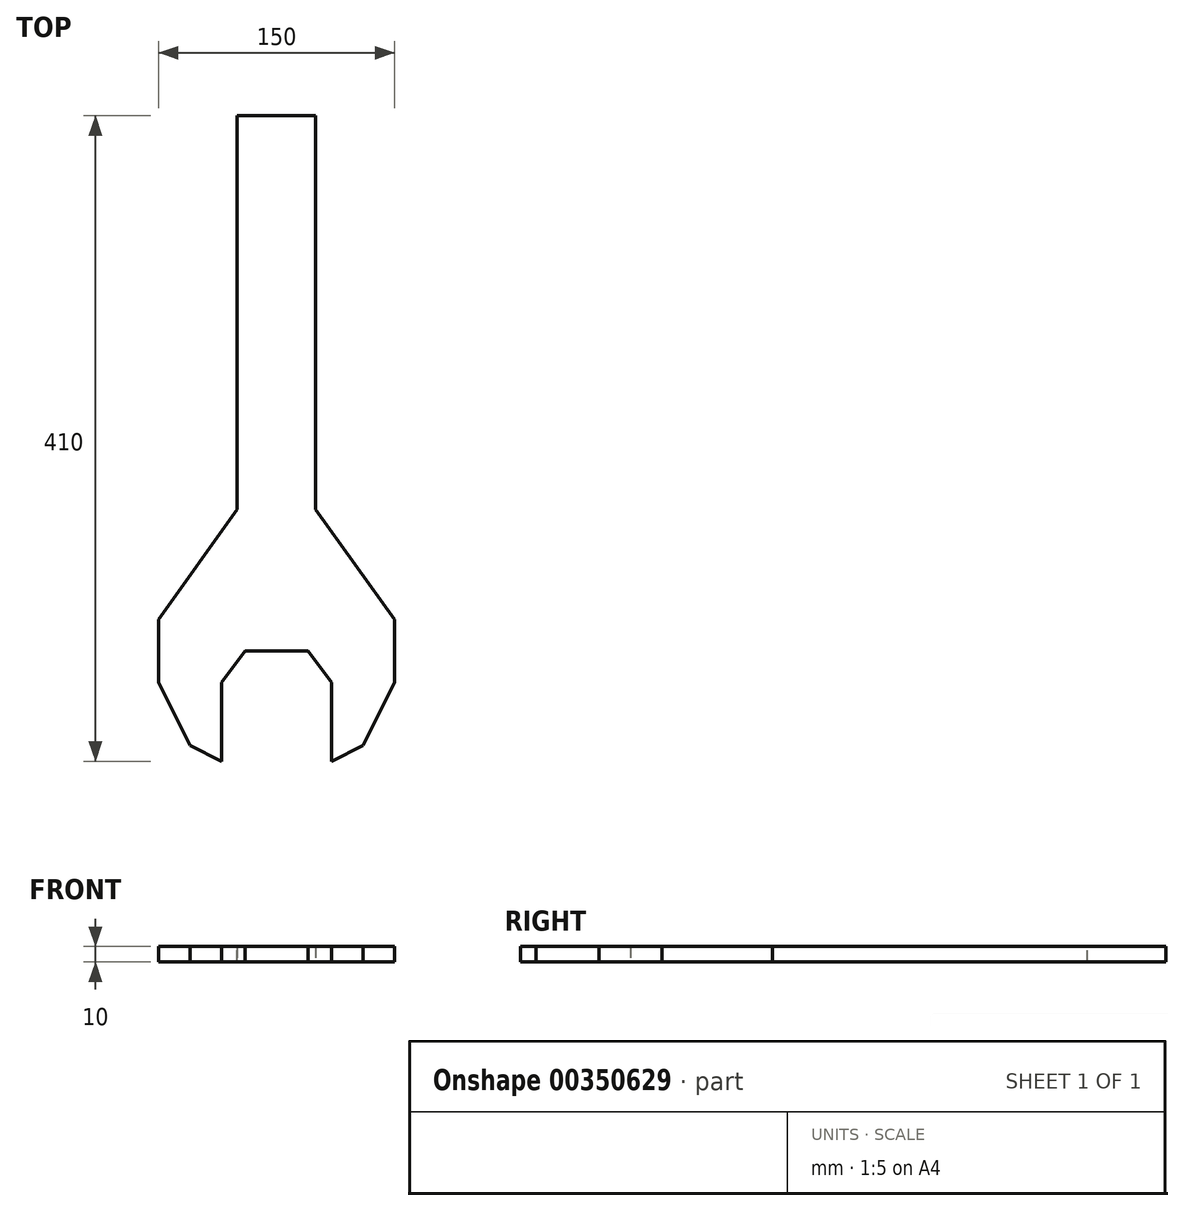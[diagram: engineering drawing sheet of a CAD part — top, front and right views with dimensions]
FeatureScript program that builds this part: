
annotation { "Feature Type Name" : "Feature", "Feature Type Description" : "" }
export const myFeature = defineFeature(function(context is Context, id is Id, definition is map)
    precondition{}
    {
        {
            var Q0;
            Q0=qCreatedBy(makeId("Top.planeOp"),FACE);
            var sketch = newSketch(context, id + "F0", { "sketchPlane" : qUnion([Q0])});
            skLineSegment(sketch, "E0", {"start": v(-20, 0) * mm, "end": v(20, 0) * mm});
            skLineSegment(sketch, "E1", {"start": v(-20, 0) * mm, "end": v(-35, -20) * mm});
            skLineSegment(sketch, "E2", {"start": v(-35, -20) * mm, "end": v(-35, -70) * mm});
            skLineSegment(sketch, "E3", {"start": v(0, 0) * mm, "end": v(0, -67.64) * mm, "construction": true});
            skLineSegment(sketch, "E4.MirrorCS", {"start": v(20, 0) * mm, "end": v(35, -20) * mm});
            skLineSegment(sketch, "E5.MirrorCS", {"start": v(35, -20) * mm, "end": v(35, -70) * mm});
            skLineSegment(sketch, "E6", {"start": v(-35, -70) * mm, "end": v(-55, -60) * mm});
            skLineSegment(sketch, "E7", {"start": v(-55, -60) * mm, "end": v(-75, -20) * mm});
            skLineSegment(sketch, "E8", {"start": v(-75, -20) * mm, "end": v(-75, 20) * mm});
            skLineSegment(sketch, "E9", {"start": v(-75, 20) * mm, "end": v(-25, 90) * mm});
            skLineSegment(sketch, "E10.MirrorCS", {"start": v(35, -70) * mm, "end": v(55, -60) * mm});
            skLineSegment(sketch, "E11.MirrorCS", {"start": v(55, -60) * mm, "end": v(75, -20) * mm});
            skLineSegment(sketch, "E12.MirrorCS", {"start": v(75, 20) * mm, "end": v(25, 90) * mm});
            skLineSegment(sketch, "E13.MirrorCS", {"start": v(75, -20) * mm, "end": v(75, 20) * mm});
            skLineSegment(sketch, "E14", {"start": v(-25, 90) * mm, "end": v(-25, 340) * mm});
            skLineSegment(sketch, "E15", {"start": v(25, 90) * mm, "end": v(25, 340) * mm});
            skLineSegment(sketch, "E16", {"start": v(25, 340) * mm, "end": v(-25, 340) * mm});
            skSolve(sketch);
        }
        {
            var Q0;
            Q0=makeQuery(id+"F0.imprint","IMPRINT",FACE,{"disambiguationData":[TD([[makeQuery(id+"F0.imprint","IMPRINT",EDGE,{"derivedFrom":sQuery(id+"F0.wireOp",EDGE,"E0")}),1.0]])]});
            extrude(context, id + "F1", {"entities" : qUnion([Q0]), "depth" : 10 * mm});
        }
        {
            var Q0;
            Q0=makeQuery(id+"F1.opExtrude","SWEPT_FACE",FACE,{"disambiguationData":[OSD([sQuery(id+"F0.wireOp",EDGE,"E14")])]});
            var sketch = newSketch(context, id + "F2", { "sketchPlane" : qUnion([Q0])});
            skLineSegment(sketch, "E17", {"start": v(-290, 0) * mm, "end": v(-290, 10) * mm});
            skSolve(sketch);
        }
        {
            var Q0;
            {var subQ0=sQuery(id+"F2.wireOp",EDGE,"E17");Q0=makeQuery(id+"F2.imprint","IMPRINT",FACE,{"disambiguationData":[TD([[makeQuery(id+"F2.imprint","IMPRINT",EDGE,{"derivedFrom":subQ0}),1.0]])]});}
            extrude(context, id + "F3", {"entities" : qUnion([Q0]), "operationType" : NewBodyOperationType.ADD, "depth" : .1 * mm});
        }
    });
